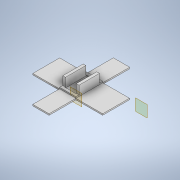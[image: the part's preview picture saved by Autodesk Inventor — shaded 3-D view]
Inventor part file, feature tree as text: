
AUTODESK INVENTOR PART (.ipt)
format: ipt  version: 2021.2 (Build 252289000, 289)  size: 205,312 bytes
history: native  units: in
note: dims shown in document units (in); Inventor stores cm internally (conversion verified against a paired STEP export)
features: extrude x12, sketch x12, plane x2
ambient origin geometry x8: Origin, YZ Plane, XZ Plane, XY Plane, X Axis, Y Axis, Z Axis, Center Point
bodies: Solid1 (feature_tree)
feature tree (26):
  extrude  "Extrusion1"  Depth=1.5906in
  extrude  "Extrusion3"  Depth=0.2in
  extrude  "Extrusion6"  Depth=0.2in
  extrude  "Extrusion7"  Depth=0.14in TaperAngle=0.0deg
  extrude  "Extrusion9"  Depth=2.0in TaperAngle=0.0deg
  plane  "Work Plane1"
  extrude  "Extrusion10"  Depth=2.0in TaperAngle=0.0deg
  plane  "Work Plane2"
  extrude  "Extrusion11"  Depth=0.2375in TaperAngle=0.0deg
  extrude  "Extrusion12"  Depth=0.1in
  extrude  "Extrusion13"  Depth=1.9875in TaperAngle=0.0deg
  extrude  "Extrusion14"  Depth=1.9875in TaperAngle=0.0deg
  extrude  "Extrusion15"  [1 undecoded]
  extrude  "Extrusion16"  [1 undecoded]
  sketch  "Sketch1"  dims[d0=0.8071in d1=1.5906in]
  sketch  "Sketch3"  dims[d2=0.2in d3=0.2in]
  sketch  "Sketch6"  dims[d4=0.2in d5=0.2in]
  sketch  "Sketch7"  dims[d6=0.9843in d7=0.0in d11=0.14in d12=0.0in]
  sketch  "Sketch9"  dims[d17=0.1in d18=2.0in d19=0.0in]
  sketch  "Sketch10"  dims[d20=2.0in d21=0.0in d24=0.3in d25=0.0in]
  sketch  "Sketch11"  dims[d26=0.2375in d27=0.0in d28=0.2375in d29=0.0in]
  sketch  "Sketch12"  dims[d30=1.9875in d31=0.0in d32=0.1in]
  sketch  "Sketch13"  dims[d33=1.9875in d34=0.0in d35=1.9875in d36=0.0in]
  sketch  "Sketch14"  dims[d37=1.9875in d38=0.0in d39=1.9875in d40=0.0in]
  sketch  "Sketch15"
  sketch  "Sketch16"
note: 2 required parameter values undecoded (feature->parameter linkage not recoverable at this tier; creation-order binding heuristic only, values carry confidence <= 0.55)
